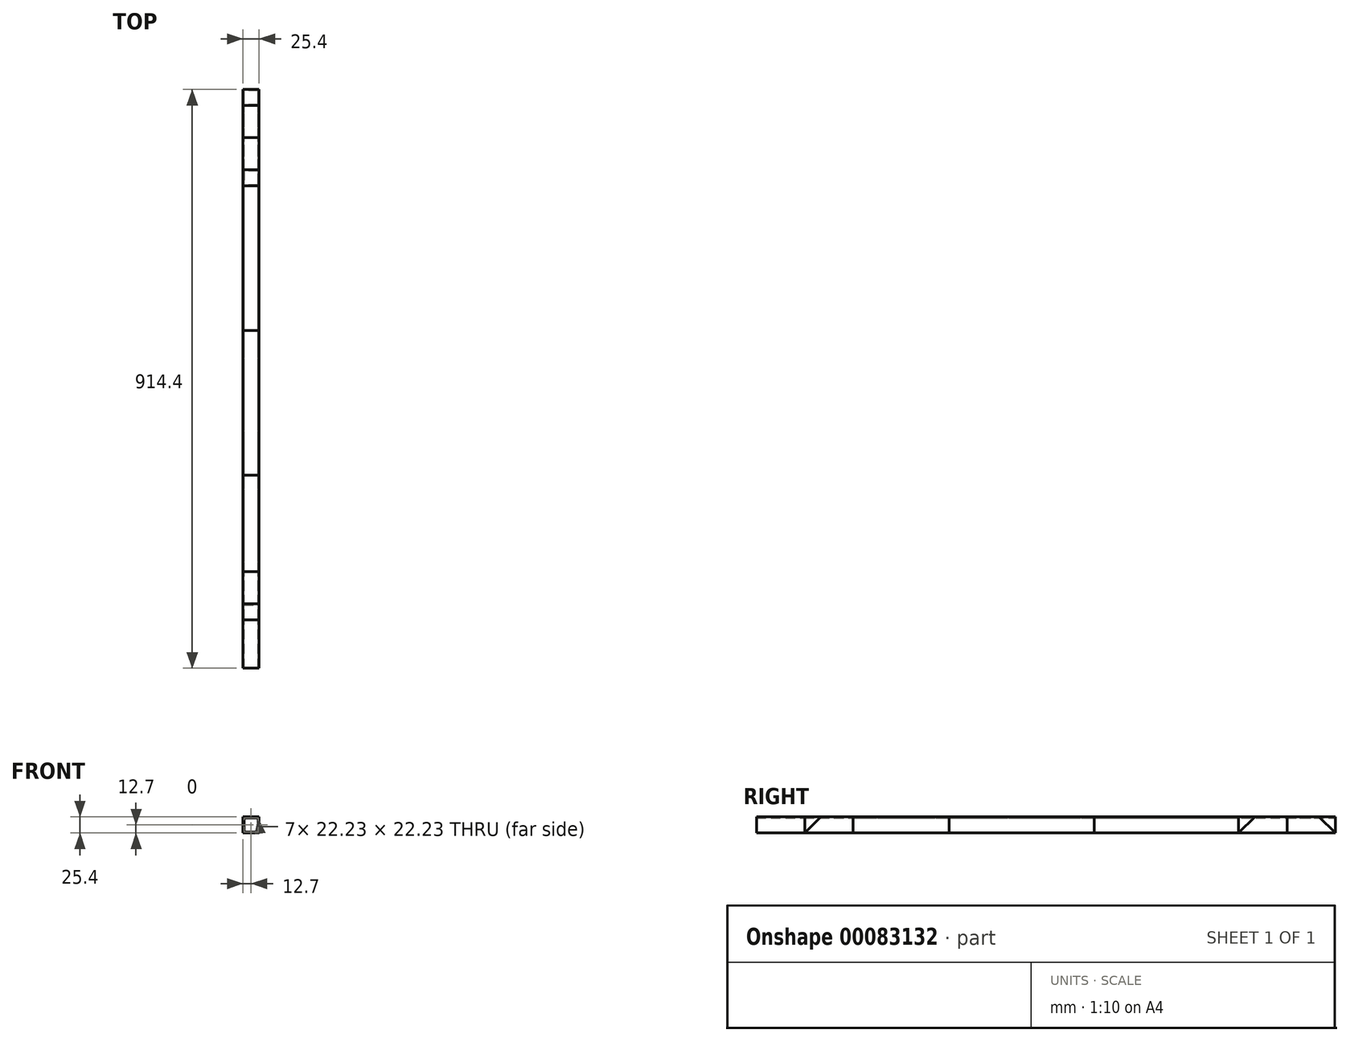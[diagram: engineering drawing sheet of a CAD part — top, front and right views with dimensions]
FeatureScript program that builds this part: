
annotation { "Feature Type Name" : "Feature", "Feature Type Description" : "" }
export const myFeature = defineFeature(function(context is Context, id is Id, definition is map)
    precondition{}
    {
        {
            var Q0;
            Q0=qCreatedBy(makeId("Front.planeOp"),FACE);
            var sketch = newSketch(context, id + "F0", { "sketchPlane" : qUnion([Q0])});
            skLineSegment(sketch, "E0.bottom", {"start": v(0, 0) * mm, "end": v(25.4, 0) * mm});
            skLineSegment(sketch, "E0.top", {"start": v(0, 25.4) * mm, "end": v(25.4, 25.4) * mm});
            skLineSegment(sketch, "E0.left", {"start": v(0, 0) * mm, "end": v(0, 25.4) * mm});
            skLineSegment(sketch, "E0.right", {"start": v(25.4, 0) * mm, "end": v(25.4, 25.4) * mm});
            skLineSegment(sketch, "E1.bottom", {"start": v(1.59, 1.59) * mm, "end": v(23.81, 1.59) * mm});
            skLineSegment(sketch, "E1.top", {"start": v(1.59, 23.81) * mm, "end": v(23.81, 23.81) * mm});
            skLineSegment(sketch, "E1.left", {"start": v(1.59, 1.59) * mm, "end": v(1.59, 23.81) * mm});
            skLineSegment(sketch, "E1.right", {"start": v(23.81, 1.59) * mm, "end": v(23.81, 23.81) * mm});
            skSolve(sketch);
        }
        {
            var Q0;
            Q0=makeQuery(id+"F0.imprint","IMPRINT",FACE,{"disambiguationData":[TD([[makeQuery(id+"F0.imprint","IMPRINT",EDGE,{"derivedFrom":sQuery(id+"F0.wireOp",EDGE,"E0.bottom")}),1.0]])]});
            extrude(context, id + "F1", {"entities" : qUnion([Q0]), "depth" : 914.4 * mm});
        }
        {
            var Q0;
            Q0=qSketchRegion(id+"F0",true);
            extrude(context, id + "F2", {"entities" : qUnion([Q0]), "depth" : 152.4 * mm});
        }
        {
            var Q0;
            Q0=qSketchRegion(id+"F0",true);
            extrude(context, id + "F3", {"entities" : qUnion([Q0]), "depth" : 381 * mm});
        }
        {
            var Q0;
            Q0=qSketchRegion(id+"F0",true);
            extrude(context, id + "F4", {"entities" : qUnion([Q0]), "depth" : 381 * mm});
        }
        {
            var Q0;
            Q0=qSketchRegion(id+"F0",true);
            extrude(context, id + "F5", {"entities" : qUnion([Q0]), "depth" : 609.6 * mm});
        }
        {
            var Q0;
            Q0=qSketchRegion(id+"F0",true);
            extrude(context, id + "F6", {"entities" : qUnion([Q0]), "depth" : 838.2 * mm});
        }
        {
            var Q0;
            Q0=qSketchRegion(id+"F0",true);
            extrude(context, id + "F7", {"entities" : qUnion([Q0]), "depth" : 76.2 * mm});
        }
        {
            var Q0;
            Q0=qSketchRegion(id+"F0",true);
            extrude(context, id + "F8", {"entities" : qUnion([Q0]), "depth" : 762 * mm});
        }
        {
            var Q0;
            Q0 = qSketchRegion(id + "F0", true);
            extrude(context, id + "F9", {"entities" : qUnion([Q0]), "depth" : 152.4 * mm});
        }
        {
            var Q0;
            Q0=makeQuery(id+"F9.opExtrude","SWEPT_FACE",FACE,{"disambiguationData":[OSD([sQuery(id+"F0.wireOp",EDGE,"E0.right")])]});
            var sketch = newSketch(context, id + "F10", { "sketchPlane" : qUnion([Q0])});
            skLineSegment(sketch, "E2", {"start": v(-152.4, 0) * mm, "end": v(-127, 25.4) * mm});
            skLineSegment(sketch, "E3", {"start": v(0, 0) * mm, "end": v(-25.4, 25.4) * mm});
            skLineSegment(sketch, "E4", {"start": v(-127, 25.4) * mm, "end": v(-152.4, 25.4) * mm});
            skLineSegment(sketch, "E5", {"start": v(-152.4, 0) * mm, "end": v(-152.4, 25.4) * mm});
            skLineSegment(sketch, "E6", {"start": v(-25.4, 25.4) * mm, "end": v(0, 25.4) * mm});
            skSolve(sketch);
        }
        {
            var Q0;
            Q0=makeQuery(id+"F10.imprint","IMPRINT",FACE,{"disambiguationData":[TD([[makeQuery(id+"F10.imprint","IMPRINT",EDGE,{"derivedFrom":sQuery(id+"F10.wireOp",EDGE,"E2")}),1.0]])]});
            var Q1;
            Q1=makeQuery(id+"F10.imprint","IMPRINT",FACE,{"disambiguationData":[TD([[makeQuery(id+"F10.imprint","IMPRINT",EDGE,{"derivedFrom":sQuery(id+"F10.wireOp",EDGE,"E3")}),-1.0]])]});
            extrude(context, id + "F11", {"entities" : qUnion([Q0, Q1]), "operationType" : NewBodyOperationType.REMOVE, "oppositeDirection" : true, "depth" : 25.4 * mm});
        }
        {
            var Q0;
            Q0=makeQuery(id+"F6.opExtrude","SWEPT_FACE",FACE,{"disambiguationData":[OSD([sQuery(id+"F0.wireOp",EDGE,"E0.right")])]});
            var sketch = newSketch(context, id + "F12", { "sketchPlane" : qUnion([Q0])});
            skLineSegment(sketch, "E7", {"start": v(-838.2, 0) * mm, "end": v(-838.2, 25.4) * mm});
            skLineSegment(sketch, "E8", {"start": v(-838.2, 25.4) * mm, "end": v(-812.8, 25.4) * mm});
            skLineSegment(sketch, "E9", {"start": v(-812.8, 25.4) * mm, "end": v(-838.2, 0) * mm});
            skLineSegment(sketch, "E10", {"start": v(0, 0) * mm, "end": v(0, 25.4) * mm});
            skLineSegment(sketch, "E11", {"start": v(0, 25.4) * mm, "end": v(-25.4, 25.4) * mm});
            skLineSegment(sketch, "E12", {"start": v(-25.4, 25.4) * mm, "end": v(0, 0) * mm});
            skSolve(sketch);
        }
        {
            var Q0;
            Q0=makeQuery(id+"F12.imprint","IMPRINT",FACE,{"disambiguationData":[TD([[makeQuery(id+"F12.imprint","IMPRINT",EDGE,{"derivedFrom":sQuery(id+"F12.wireOp",EDGE,"E10")}),1.0]])]});
            var Q1;
            Q1=makeQuery(id+"F12.imprint","IMPRINT",FACE,{"disambiguationData":[TD([[makeQuery(id+"F12.imprint","IMPRINT",EDGE,{"derivedFrom":sQuery(id+"F12.wireOp",EDGE,"E7")}),-1.0]])]});
            extrude(context, id + "F13", {"entities" : qUnion([Q0, Q1]), "operationType" : NewBodyOperationType.REMOVE, "oppositeDirection" : true, "depth" : 25.4 * mm});
        }
        {
            var Q0;
            Q0 = qSketchRegion(id + "F0", true);
            extrude(context, id + "F14", {"entities" : qUnion([Q0]), "depth" : 838.2 * mm});
        }
    });
